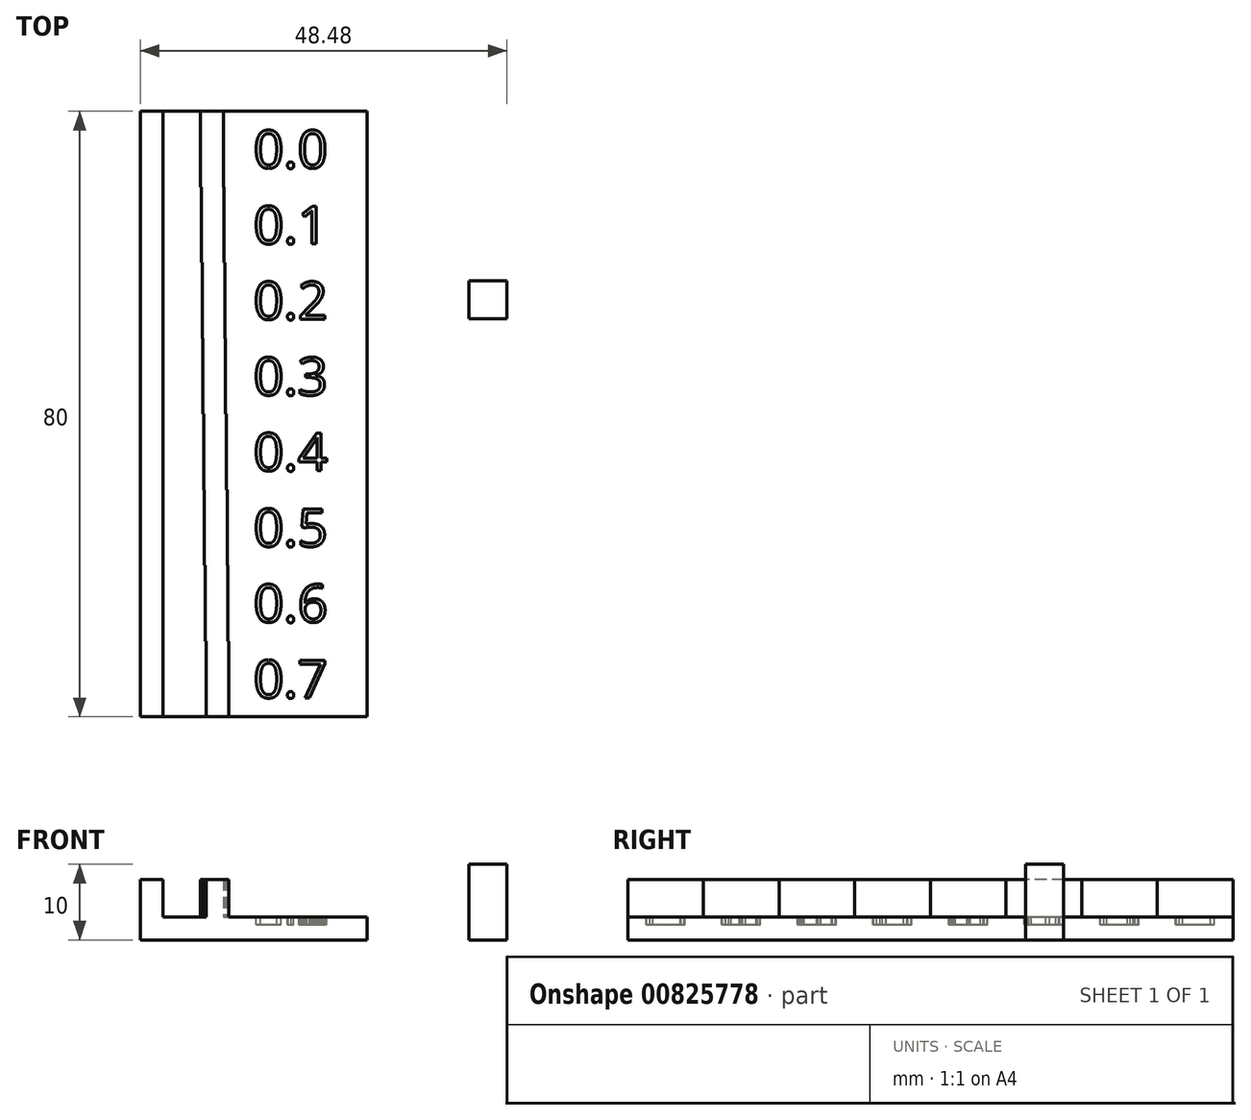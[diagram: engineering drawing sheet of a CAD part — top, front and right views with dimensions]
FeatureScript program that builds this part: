
annotation { "Feature Type Name" : "Feature", "Feature Type Description" : "" }
export const myFeature = defineFeature(function(context is Context, id is Id, definition is map)
    precondition{}
    {
        {
            var Q0;
            Q0=qCreatedBy(makeId("Top.planeOp"),FACE);
            var sketch = newSketch(context, id + "F0", { "sketchPlane" : qUnion([Q0])});
            skLineSegment(sketch, "E0.bottom", {"start": v(-15, 40) * mm, "end": v(15, 40) * mm});
            skLineSegment(sketch, "E0.top", {"start": v(-15, -40) * mm, "end": v(15, -40) * mm});
            skLineSegment(sketch, "E0.left", {"start": v(-15, 40) * mm, "end": v(-15, -40) * mm});
            skLineSegment(sketch, "E0.right", {"start": v(15, 40) * mm, "end": v(15, -40) * mm});
            skPoint(sketch, "E1", {"position": v(15, 0) * mm});
            skPoint(sketch, "E2", {"position": v(0, 40) * mm});
            skSolve(sketch);
        }
        {
            var Q0;
            Q0=makeQuery(id+"F0.imprint","IMPRINT",FACE,{"disambiguationData":[TD([[makeQuery(id+"F0.imprint","IMPRINT",EDGE,{"derivedFrom":sQuery(id+"F0.wireOp",EDGE,"E0.bottom")}),-1.0]])]});
            extrude(context, id + "F1", {"entities" : qUnion([Q0]), "depth" : 3 * mm, "offsetDistance" : 25 * mm});
        }
        {
            var Q0;
            Q0=makeQuery(id+"F1.opExtrude","CAP_FACE",FACE,{"disambiguationData":[OSD([sQuery(id+"F0.wireOp",EDGE,"E0.bottom"),sQuery(id+"F0.wireOp",EDGE,"E0.top"),sQuery(id+"F0.wireOp",EDGE,"E0.left"),sQuery(id+"F0.wireOp",EDGE,"E0.right")])],"isStart":false});
            var sketch = newSketch(context, id + "F2", { "sketchPlane" : qUnion([Q0])});
            skLineSegment(sketch, "E3", {"start": v(-15, 40) * mm, "end": v(-15, -40) * mm});
            skLineSegment(sketch, "E4", {"start": v(-15, -40) * mm, "end": v(-12, -40) * mm});
            skLineSegment(sketch, "E5", {"start": v(-12, -40) * mm, "end": v(-12, 40) * mm});
            skLineSegment(sketch, "E6", {"start": v(-12, 40) * mm, "end": v(-15, 40) * mm});
            skLineSegment(sketch, "E7", {"start": v(-7, 40) * mm, "end": v(-7, 30) * mm});
            skLineSegment(sketch, "E8", {"start": v(-7, 30) * mm, "end": v(-4, 30) * mm});
            skLineSegment(sketch, "E9", {"start": v(-4, 30) * mm, "end": v(-4, 40) * mm});
            skLineSegment(sketch, "E10", {"start": v(-4, 40) * mm, "end": v(-7, 40) * mm});
            skLineSegment(sketch, "E11", {"start": v(-6.9, 30) * mm, "end": v(-6.9, 20) * mm});
            skLineSegment(sketch, "E12", {"start": v(-6.9, 20) * mm, "end": v(-3.9, 20) * mm});
            skLineSegment(sketch, "E13", {"start": v(-3.9, 20) * mm, "end": v(-3.9, 30) * mm});
            skLineSegment(sketch, "E14", {"start": v(-3.9, 30) * mm, "end": v(-6.9, 30) * mm});
            skLineSegment(sketch, "E15.bottom", {"start": v(-6.8, 20) * mm, "end": v(-3.8, 20) * mm});
            skLineSegment(sketch, "E15.top", {"start": v(-6.8, 10) * mm, "end": v(-3.8, 10) * mm});
            skLineSegment(sketch, "E15.left", {"start": v(-6.8, 20) * mm, "end": v(-6.8, 10) * mm});
            skLineSegment(sketch, "E15.right", {"start": v(-3.8, 20) * mm, "end": v(-3.8, 10) * mm});
            skLineSegment(sketch, "E16.bottom", {"start": v(-6.7, 10) * mm, "end": v(-3.7, 10) * mm});
            skLineSegment(sketch, "E16.top", {"start": v(-6.7, 0) * mm, "end": v(-3.7, 0) * mm});
            skLineSegment(sketch, "E16.left", {"start": v(-6.7, 10) * mm, "end": v(-6.7, 0) * mm});
            skLineSegment(sketch, "E16.right", {"start": v(-3.7, 10) * mm, "end": v(-3.7, 0) * mm});
            skLineSegment(sketch, "E17.bottom", {"start": v(-6.6, 0) * mm, "end": v(-3.6, 0) * mm});
            skLineSegment(sketch, "E17.top", {"start": v(-6.6, -10) * mm, "end": v(-3.6, -10) * mm});
            skLineSegment(sketch, "E17.left", {"start": v(-6.6, 0) * mm, "end": v(-6.6, -10) * mm});
            skLineSegment(sketch, "E17.right", {"start": v(-3.6, 0) * mm, "end": v(-3.6, -10) * mm});
            skLineSegment(sketch, "E18.bottom", {"start": v(-6.5, -10) * mm, "end": v(-3.5, -10) * mm});
            skLineSegment(sketch, "E18.top", {"start": v(-6.5, -20) * mm, "end": v(-3.5, -20) * mm});
            skLineSegment(sketch, "E18.left", {"start": v(-6.5, -10) * mm, "end": v(-6.5, -20) * mm});
            skLineSegment(sketch, "E18.right", {"start": v(-3.5, -10) * mm, "end": v(-3.5, -20) * mm});
            skLineSegment(sketch, "E19.bottom", {"start": v(-6.4, -20) * mm, "end": v(-3.4, -20) * mm});
            skLineSegment(sketch, "E19.top", {"start": v(-6.4, -30) * mm, "end": v(-3.4, -30) * mm});
            skLineSegment(sketch, "E19.left", {"start": v(-6.4, -20) * mm, "end": v(-6.4, -30) * mm});
            skLineSegment(sketch, "E19.right", {"start": v(-3.4, -20) * mm, "end": v(-3.4, -30) * mm});
            skLineSegment(sketch, "E20.bottom", {"start": v(-6.3, -30) * mm, "end": v(-3.3, -30) * mm});
            skLineSegment(sketch, "E20.top", {"start": v(-6.3, -40) * mm, "end": v(-3.3, -40) * mm});
            skLineSegment(sketch, "E20.left", {"start": v(-6.3, -30) * mm, "end": v(-6.3, -40) * mm});
            skLineSegment(sketch, "E20.right", {"start": v(-3.3, -30) * mm, "end": v(-3.3, -40) * mm});
            skSolve(sketch);
        }
        {
            var Q0;
            Q0=makeQuery(id+"F2.imprint","IMPRINT",FACE,{"disambiguationData":[TD([[makeQuery(id+"F2.imprint","IMPRINT",EDGE,{"derivedFrom":sQuery(id+"F2.wireOp",EDGE,"E7")}),1.0]])]});
            var Q1;
            {var subQ4=sQuery(id+"F2.wireOp",EDGE,"E11");Q1=makeQuery(id+"F2.imprint","IMPRINT",FACE,{"disambiguationData":[TD([[makeQuery(id+"F2.imprint","IMPRINT",EDGE,{"derivedFrom":subQ4}),1.0]])]});}
            var Q2;
            {var subQ1=sQuery(id+"F2.wireOp",EDGE,"E15.top");Q2=makeQuery(id+"F2.imprint","IMPRINT",FACE,{"disambiguationData":[TD([[makeQuery(id+"F2.imprint","IMPRINT",EDGE,{"derivedFrom":subQ1}),1.0]])]});}
            var Q3;
            {var subQ1=sQuery(id+"F2.wireOp",EDGE,"E16.top");Q3=makeQuery(id+"F2.imprint","IMPRINT",FACE,{"disambiguationData":[TD([[makeQuery(id+"F2.imprint","IMPRINT",EDGE,{"derivedFrom":subQ1}),1.0]])]});}
            var Q4;
            {var subQ1=sQuery(id+"F2.wireOp",EDGE,"E17.top");Q4=makeQuery(id+"F2.imprint","IMPRINT",FACE,{"disambiguationData":[TD([[makeQuery(id+"F2.imprint","IMPRINT",EDGE,{"derivedFrom":subQ1}),1.0]])]});}
            var Q5;
            {var subQ1=sQuery(id+"F2.wireOp",EDGE,"E18.top");Q5=makeQuery(id+"F2.imprint","IMPRINT",FACE,{"disambiguationData":[TD([[makeQuery(id+"F2.imprint","IMPRINT",EDGE,{"derivedFrom":subQ1}),1.0]])]});}
            var Q6;
            {var subQ1=sQuery(id+"F2.wireOp",EDGE,"E19.top");Q6=makeQuery(id+"F2.imprint","IMPRINT",FACE,{"disambiguationData":[TD([[makeQuery(id+"F2.imprint","IMPRINT",EDGE,{"derivedFrom":subQ1}),1.0]])]});}
            var Q7;
            Q7=makeQuery(id+"F2.imprint","IMPRINT",FACE,{"disambiguationData":[TD([[makeQuery(id+"F2.imprint","IMPRINT",EDGE,{"derivedFrom":sQuery(id+"F2.wireOp",EDGE,"E20.top")}),1.0]])]});
            var Q8;
            Q8=makeQuery(id+"F2.imprint","IMPRINT",FACE,{"disambiguationData":[TD([[makeQuery(id+"F2.imprint","IMPRINT",EDGE,{"derivedFrom":sQuery(id+"F2.wireOp",EDGE,"E4")}),1.0]])]});
            extrude(context, id + "F3", {"entities" : qUnion([Q0, Q1, Q2, Q3, Q4, Q5, Q6, Q7, Q8]), "operationType" : NewBodyOperationType.ADD, "depth" : 5 * mm, "offsetDistance" : 25 * mm});
        }
        {
            var Q0;
            {var subQ0=sQuery(id+"F0.wireOp",EDGE,"E0.bottom");var subQ1=sQuery(id+"F0.wireOp",EDGE,"E0.right");var subQ2=sQuery(id+"F0.wireOp",EDGE,"E0.top");Q0=makeQuery(id+"F3.boolean.opBoolean","SPLIT",FACE,{"disambiguationData":[TD([makeQuery(id+"F1.opExtrude","SWEPT_FACE",FACE,{"disambiguationData":[OSD([subQ1])]})])],"derivedFrom":makeQuery(id+"F1.opExtrude","CAP_FACE",FACE,{"disambiguationData":[OSD([subQ0,subQ2,sQuery(id+"F0.wireOp",EDGE,"E0.left"),subQ1])],"isStart":false})});}
            var sketch = newSketch(context, id + "F4", { "sketchPlane" : qUnion([Q0])});
            skText(sketch, "E21", { "text": "0.0", "fontName": "OpenSans-Regular.ttf"});
            skText(sketch, "E22", { "text": "0.1\n", "fontName": "OpenSans-Regular.ttf"});
            skText(sketch, "E23", { "text": "0.2", "fontName": "OpenSans-Regular.ttf"});
            skText(sketch, "E24", { "text": "0.3", "fontName": "OpenSans-Regular.ttf"});
            skText(sketch, "E25", { "text": "0.4", "fontName": "OpenSans-Regular.ttf"});
            skText(sketch, "E26", { "text": "0.5", "fontName": "OpenSans-Regular.ttf"});
            skText(sketch, "E27", { "text": "0.6", "fontName": "OpenSans-Regular.ttf"});
            skText(sketch, "E28", { "text": "0.7", "fontName": "OpenSans-Regular.ttf"});
            const initialGuessF4  = {"E21": [0, 0.0325, 1, 0, 0.005], "E22": [0, 0.0225, 1, 0, 0.005], "E23": [0, 0.0125, 1, 0, 0.005], "E24": [0, 0.0025, 1, 0, 0.005], "E25": [0, -0.0075, 1, 0, 0.005], "E26": [0, -0.0175, 1, 0, 0.005], "E27": [0, -0.0275, 1, 0, 0.005], "E28": [0, -0.0375, 1, 0, 0.005]};
            skSetInitialGuess(sketch, initialGuessF4);
            skSolve(sketch);
        }
        {
            var Q0;
            Q0 = qSketchRegion(id + "F4", true);
            extrude(context, id + "F5", {"entities" : qUnion([Q0]), "operationType" : NewBodyOperationType.REMOVE, "oppositeDirection" : true, "depth" : 1 * mm, "offsetDistance" : 25 * mm});
        }
        {
            var Q0;
            Q0=qCreatedBy(makeId("Top.planeOp"),FACE);
            var sketch = newSketch(context, id + "F6", { "sketchPlane" : qUnion([Q0])});
            skLineSegment(sketch, "E29.bottom", {"start": v(28.48, 17.59) * mm, "end": v(33.48, 17.59) * mm});
            skLineSegment(sketch, "E29.top", {"start": v(28.48, 12.59) * mm, "end": v(33.48, 12.59) * mm});
            skLineSegment(sketch, "E29.left", {"start": v(28.48, 17.59) * mm, "end": v(28.48, 12.59) * mm});
            skLineSegment(sketch, "E29.right", {"start": v(33.48, 17.59) * mm, "end": v(33.48, 12.59) * mm});
            skSolve(sketch);
        }
        {
            var Q0;
            Q0 = qSketchRegion(id + "F6", true);
            extrude(context, id + "F7", {"entities" : qUnion([Q0]), "depth" : 10 * mm, "offsetDistance" : 25 * mm});
        }
    });
